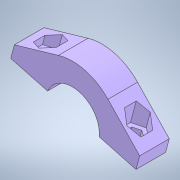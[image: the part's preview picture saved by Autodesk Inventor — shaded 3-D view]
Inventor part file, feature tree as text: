
AUTODESK INVENTOR PART (.ipt)
format: ipt  version: 2021.2 (Build 252289000, 289)  size: 167,424 bytes
history: native  units: mm
features: other x4, fillet x1
ambient origin geometry x8: Origin, YZ Plane, XZ Plane, XY Plane, X Axis, Y Axis, Z Axis, Center Point
bodies: Body1 (feature_tree)
feature tree (5):
  other  "Твёрдое тело.ipt"
  fillet  "Сопряжение2"  Radius=10.0mm
  other  "Скобка 1::Твёрдое тело.ipt"
  other  "Элемент создания тегов1"
  other  "Твердое тело1"
